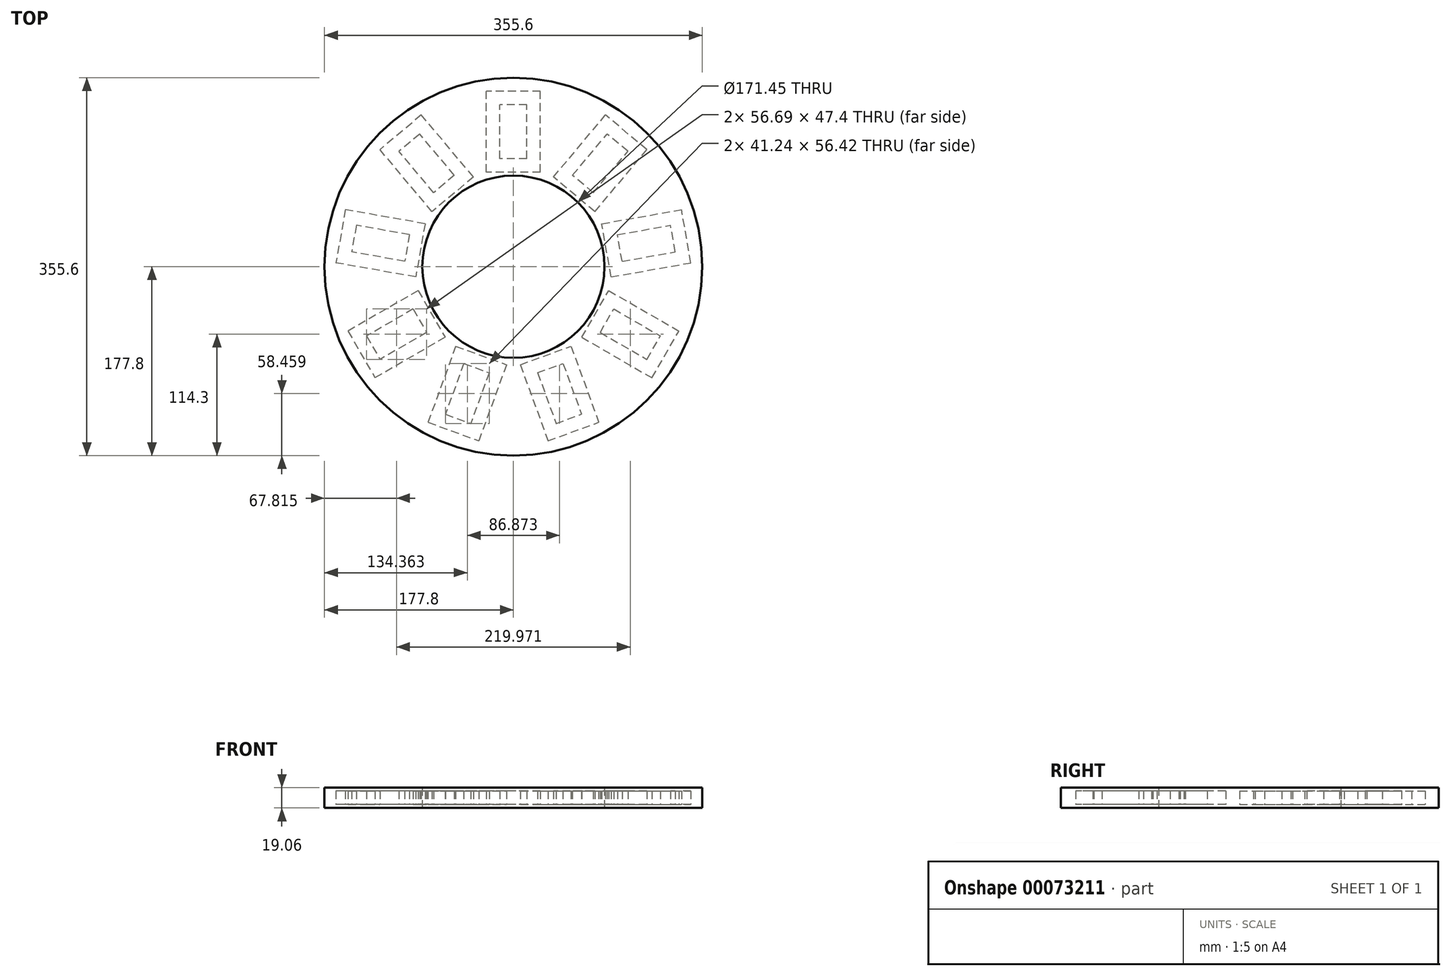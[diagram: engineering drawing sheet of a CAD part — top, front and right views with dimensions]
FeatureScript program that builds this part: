
annotation { "Feature Type Name" : "Feature", "Feature Type Description" : "" }
export const myFeature = defineFeature(function(context is Context, id is Id, definition is map)
    precondition{}
    {
        {
            var Q0;
            Q0=qCreatedBy(makeId("Top.planeOp"),FACE);
            var sketch = newSketch(context, id + "F0", { "sketchPlane" : qUnion([Q0])});
            skCircle(sketch, "E0", {"center": v(0, 0) * mm, "radius": 85.73 * mm, "construction": true});
            skCircle(sketch, "E1", {"center": v(0, 0) * mm, "radius": 177.8 * mm, "construction": true});
            skCircle(sketch, "E2", {"center": v(0, 0) * mm, "radius": 101.6 * mm, "construction": true});
            skCircle(sketch, "E3", {"center": v(0, 0) * mm, "radius": 152.4 * mm, "construction": true});
            skLineSegment(sketch, "E4.rect.bottom", {"start": v(12.7, 101.6) * mm, "end": v(-12.7, 101.6) * mm});
            skLineSegment(sketch, "E4.rect.top", {"start": v(12.7, 152.4) * mm, "end": v(-12.7, 152.4) * mm});
            skLineSegment(sketch, "E4.rect.left", {"start": v(12.7, 101.6) * mm, "end": v(12.7, 152.4) * mm});
            skLineSegment(sketch, "E4.rect.right", {"start": v(-12.7, 101.6) * mm, "end": v(-12.7, 152.4) * mm});
            skPoint(sketch, "E4.rect.middle", {"position": v(0, 127) * mm});
            skLineSegment(sketch, "E5.rect.bottom", {"start": v(25.4, 88.9) * mm, "end": v(-25.4, 88.9) * mm});
            skLineSegment(sketch, "E5.rect.top", {"start": v(25.4, 165.1) * mm, "end": v(-25.4, 165.1) * mm});
            skLineSegment(sketch, "E5.rect.left", {"start": v(25.4, 88.9) * mm, "end": v(25.4, 165.1) * mm});
            skLineSegment(sketch, "E5.rect.right", {"start": v(-25.4, 88.9) * mm, "end": v(-25.4, 165.1) * mm});
            skLineSegment(sketch, "E6.1.0", {"start": v(-37.69, 84.43) * mm, "end": v(-76.6, 51.77) * mm});
            skLineSegment(sketch, "E6.1.1", {"start": v(-86.67, 142.8) * mm, "end": v(-125.58, 110.15) * mm});
            skLineSegment(sketch, "E6.1.2", {"start": v(-37.69, 84.43) * mm, "end": v(-86.67, 142.8) * mm});
            skLineSegment(sketch, "E6.1.3", {"start": v(-76.6, 51.77) * mm, "end": v(-125.58, 110.15) * mm});
            skPoint(sketch, "E6.1.4", {"position": v(-81.63, 97.29) * mm});
            skPoint(sketch, "E6.1.5", {"position": v(-81.63, 97.29) * mm});
            skLineSegment(sketch, "E6.2.0", {"start": v(-83.14, 40.45) * mm, "end": v(-91.96, -9.58) * mm});
            skLineSegment(sketch, "E6.2.1", {"start": v(-158.18, 53.68) * mm, "end": v(-167, 3.66) * mm});
            skLineSegment(sketch, "E6.2.2", {"start": v(-83.14, 40.45) * mm, "end": v(-158.18, 53.68) * mm});
            skLineSegment(sketch, "E6.2.3", {"start": v(-91.96, -9.58) * mm, "end": v(-167, 3.66) * mm});
            skPoint(sketch, "E6.2.4", {"position": v(-125.07, 22.05) * mm});
            skPoint(sketch, "E6.2.5", {"position": v(-125.07, 22.05) * mm});
            skLineSegment(sketch, "E6.3.0", {"start": v(-89.69, -22.45) * mm, "end": v(-64.29, -66.45) * mm});
            skLineSegment(sketch, "E6.3.1", {"start": v(-155.68, -60.55) * mm, "end": v(-130.28, -104.55) * mm});
            skLineSegment(sketch, "E6.3.2", {"start": v(-89.69, -22.45) * mm, "end": v(-155.68, -60.55) * mm});
            skLineSegment(sketch, "E6.3.3", {"start": v(-64.29, -66.45) * mm, "end": v(-130.28, -104.55) * mm});
            skPoint(sketch, "E6.3.4", {"position": v(-109.99, -63.5) * mm});
            skPoint(sketch, "E6.3.5", {"position": v(-109.99, -63.5) * mm});
            skLineSegment(sketch, "E6.4.0", {"start": v(-54.27, -74.85) * mm, "end": v(-6.54, -92.23) * mm});
            skLineSegment(sketch, "E6.4.1", {"start": v(-80.34, -146.46) * mm, "end": v(-32.6, -163.83) * mm});
            skLineSegment(sketch, "E6.4.2", {"start": v(-54.27, -74.85) * mm, "end": v(-80.34, -146.46) * mm});
            skLineSegment(sketch, "E6.4.3", {"start": v(-6.54, -92.23) * mm, "end": v(-32.6, -163.83) * mm});
            skPoint(sketch, "E6.4.4", {"position": v(-43.44, -119.34) * mm});
            skPoint(sketch, "E6.4.5", {"position": v(-43.44, -119.34) * mm});
            skLineSegment(sketch, "E6.5.0", {"start": v(6.54, -92.23) * mm, "end": v(54.27, -74.85) * mm});
            skLineSegment(sketch, "E6.5.1", {"start": v(32.6, -163.83) * mm, "end": v(80.34, -146.46) * mm});
            skLineSegment(sketch, "E6.5.2", {"start": v(6.54, -92.23) * mm, "end": v(32.6, -163.83) * mm});
            skLineSegment(sketch, "E6.5.3", {"start": v(54.27, -74.85) * mm, "end": v(80.34, -146.46) * mm});
            skPoint(sketch, "E6.5.4", {"position": v(43.44, -119.34) * mm});
            skPoint(sketch, "E6.5.5", {"position": v(43.44, -119.34) * mm});
            skLineSegment(sketch, "E6.6.0", {"start": v(64.29, -66.45) * mm, "end": v(89.69, -22.45) * mm});
            skLineSegment(sketch, "E6.6.1", {"start": v(130.28, -104.55) * mm, "end": v(155.68, -60.55) * mm});
            skLineSegment(sketch, "E6.6.2", {"start": v(64.29, -66.45) * mm, "end": v(130.28, -104.55) * mm});
            skLineSegment(sketch, "E6.6.3", {"start": v(89.69, -22.45) * mm, "end": v(155.68, -60.55) * mm});
            skPoint(sketch, "E6.6.4", {"position": v(109.99, -63.5) * mm});
            skPoint(sketch, "E6.6.5", {"position": v(109.99, -63.5) * mm});
            skLineSegment(sketch, "E6.7.0", {"start": v(91.96, -9.58) * mm, "end": v(83.14, 40.45) * mm});
            skLineSegment(sketch, "E6.7.1", {"start": v(167, 3.66) * mm, "end": v(158.18, 53.68) * mm});
            skLineSegment(sketch, "E6.7.2", {"start": v(91.96, -9.58) * mm, "end": v(167, 3.66) * mm});
            skLineSegment(sketch, "E6.7.3", {"start": v(83.14, 40.45) * mm, "end": v(158.18, 53.68) * mm});
            skPoint(sketch, "E6.7.4", {"position": v(125.07, 22.05) * mm});
            skPoint(sketch, "E6.7.5", {"position": v(125.07, 22.05) * mm});
            skLineSegment(sketch, "E6.8.0", {"start": v(76.6, 51.77) * mm, "end": v(37.69, 84.43) * mm});
            skLineSegment(sketch, "E6.8.1", {"start": v(125.58, 110.15) * mm, "end": v(86.67, 142.8) * mm});
            skLineSegment(sketch, "E6.8.2", {"start": v(76.6, 51.77) * mm, "end": v(125.58, 110.15) * mm});
            skLineSegment(sketch, "E6.8.3", {"start": v(37.69, 84.43) * mm, "end": v(86.67, 142.8) * mm});
            skPoint(sketch, "E6.8.4", {"position": v(81.63, 97.29) * mm});
            skPoint(sketch, "E6.8.5", {"position": v(81.63, 97.29) * mm});
            skLineSegment(sketch, "E7.1.0", {"start": v(-88.23, 124.9) * mm, "end": v(-107.69, 108.58) * mm});
            skLineSegment(sketch, "E7.1.1", {"start": v(-75.04, 69.67) * mm, "end": v(-107.69, 108.58) * mm});
            skLineSegment(sketch, "E7.1.2", {"start": v(-55.58, 86) * mm, "end": v(-88.23, 124.9) * mm});
            skLineSegment(sketch, "E7.1.3", {"start": v(-55.58, 86) * mm, "end": v(-75.04, 69.67) * mm});
            skLineSegment(sketch, "E7.2.0", {"start": v(-147.88, 38.97) * mm, "end": v(-152.3, 13.96) * mm});
            skLineSegment(sketch, "E7.2.1", {"start": v(-102.26, 5.14) * mm, "end": v(-152.3, 13.96) * mm});
            skLineSegment(sketch, "E7.2.2", {"start": v(-97.85, 30.15) * mm, "end": v(-147.88, 38.97) * mm});
            skLineSegment(sketch, "E7.2.3", {"start": v(-97.85, 30.15) * mm, "end": v(-102.26, 5.14) * mm});
            skLineSegment(sketch, "E7.3.0", {"start": v(-138.33, -65.2) * mm, "end": v(-125.63, -87.2) * mm});
            skLineSegment(sketch, "E7.3.1", {"start": v(-81.64, -61.8) * mm, "end": v(-125.63, -87.2) * mm});
            skLineSegment(sketch, "E7.3.2", {"start": v(-94.34, -39.8) * mm, "end": v(-138.33, -65.2) * mm});
            skLineSegment(sketch, "E7.3.3", {"start": v(-94.34, -39.8) * mm, "end": v(-81.64, -61.8) * mm});
            skLineSegment(sketch, "E7.4.0", {"start": v(-64.06, -138.87) * mm, "end": v(-40.19, -147.55) * mm});
            skLineSegment(sketch, "E7.4.1", {"start": v(-22.82, -99.82) * mm, "end": v(-40.19, -147.55) * mm});
            skLineSegment(sketch, "E7.4.2", {"start": v(-46.68, -91.13) * mm, "end": v(-64.06, -138.87) * mm});
            skLineSegment(sketch, "E7.4.3", {"start": v(-46.68, -91.13) * mm, "end": v(-22.82, -99.82) * mm});
            skLineSegment(sketch, "E7.5.0", {"start": v(40.19, -147.55) * mm, "end": v(64.06, -138.87) * mm});
            skLineSegment(sketch, "E7.5.1", {"start": v(46.68, -91.13) * mm, "end": v(64.06, -138.87) * mm});
            skLineSegment(sketch, "E7.5.2", {"start": v(22.82, -99.82) * mm, "end": v(40.19, -147.55) * mm});
            skLineSegment(sketch, "E7.5.3", {"start": v(22.82, -99.82) * mm, "end": v(46.68, -91.13) * mm});
            skLineSegment(sketch, "E7.6.0", {"start": v(125.63, -87.2) * mm, "end": v(138.33, -65.2) * mm});
            skLineSegment(sketch, "E7.6.1", {"start": v(94.34, -39.8) * mm, "end": v(138.33, -65.2) * mm});
            skLineSegment(sketch, "E7.6.2", {"start": v(81.64, -61.8) * mm, "end": v(125.63, -87.2) * mm});
            skLineSegment(sketch, "E7.6.3", {"start": v(81.64, -61.8) * mm, "end": v(94.34, -39.8) * mm});
            skLineSegment(sketch, "E7.7.0", {"start": v(152.3, 13.96) * mm, "end": v(147.88, 38.97) * mm});
            skLineSegment(sketch, "E7.7.1", {"start": v(97.85, 30.15) * mm, "end": v(147.88, 38.97) * mm});
            skLineSegment(sketch, "E7.7.2", {"start": v(102.26, 5.14) * mm, "end": v(152.3, 13.96) * mm});
            skLineSegment(sketch, "E7.7.3", {"start": v(102.26, 5.14) * mm, "end": v(97.85, 30.15) * mm});
            skLineSegment(sketch, "E7.8.0", {"start": v(107.69, 108.58) * mm, "end": v(88.23, 124.9) * mm});
            skLineSegment(sketch, "E7.8.1", {"start": v(55.58, 86) * mm, "end": v(88.23, 124.9) * mm});
            skLineSegment(sketch, "E7.8.2", {"start": v(75.04, 69.67) * mm, "end": v(107.69, 108.58) * mm});
            skLineSegment(sketch, "E7.8.3", {"start": v(75.04, 69.67) * mm, "end": v(55.58, 86) * mm});
            skSolve(sketch);
        }
        {
            var Q0;
            Q0=makeQuery(id+"F0.imprint","IMPRINT",FACE,{"disambiguationData":[TD([[makeQuery(id+"F0.imprint","IMPRINT",EDGE,{"derivedFrom":sQuery(id+"F0.wireOp",EDGE,"E6.1.0")}),-1.0]])]});
            var Q1;
            Q1=makeQuery(id+"F0.imprint","IMPRINT",FACE,{"disambiguationData":[TD([[makeQuery(id+"F0.imprint","IMPRINT",EDGE,{"derivedFrom":sQuery(id+"F0.wireOp",EDGE,"E4.rect.bottom")}),1.0]])]});
            var Q2;
            Q2=makeQuery(id+"F0.imprint","IMPRINT",FACE,{"disambiguationData":[TD([[makeQuery(id+"F0.imprint","IMPRINT",EDGE,{"derivedFrom":sQuery(id+"F0.wireOp",EDGE,"E6.9.0")}),-1.0]])]});
            var Q3;
            Q3=makeQuery(id+"F0.imprint","IMPRINT",FACE,{"disambiguationData":[TD([[makeQuery(id+"F0.imprint","IMPRINT",EDGE,{"derivedFrom":sQuery(id+"F0.wireOp",EDGE,"E6.2.0")}),-1.0]])]});
            var Q4;
            Q4=makeQuery(id+"F0.imprint","IMPRINT",FACE,{"disambiguationData":[TD([[makeQuery(id+"F0.imprint","IMPRINT",EDGE,{"derivedFrom":sQuery(id+"F0.wireOp",EDGE,"E6.8.0")}),-1.0]])]});
            var Q5;
            Q5=makeQuery(id+"F0.imprint","IMPRINT",FACE,{"disambiguationData":[TD([[makeQuery(id+"F0.imprint","IMPRINT",EDGE,{"derivedFrom":sQuery(id+"F0.wireOp",EDGE,"E6.7.0")}),-1.0]])]});
            var Q6;
            Q6=makeQuery(id+"F0.imprint","IMPRINT",FACE,{"disambiguationData":[TD([[makeQuery(id+"F0.imprint","IMPRINT",EDGE,{"derivedFrom":sQuery(id+"F0.wireOp",EDGE,"E6.6.0")}),-1.0]])]});
            var Q7;
            Q7=makeQuery(id+"F0.imprint","IMPRINT",FACE,{"disambiguationData":[TD([[makeQuery(id+"F0.imprint","IMPRINT",EDGE,{"derivedFrom":sQuery(id+"F0.wireOp",EDGE,"E6.5.0")}),-1.0]])]});
            var Q8;
            Q8=makeQuery(id+"F0.imprint","IMPRINT",FACE,{"disambiguationData":[TD([[makeQuery(id+"F0.imprint","IMPRINT",EDGE,{"derivedFrom":sQuery(id+"F0.wireOp",EDGE,"E6.4.0")}),-1.0]])]});
            var Q9;
            Q9=makeQuery(id+"F0.imprint","IMPRINT",FACE,{"disambiguationData":[TD([[makeQuery(id+"F0.imprint","IMPRINT",EDGE,{"derivedFrom":sQuery(id+"F0.wireOp",EDGE,"E6.3.0")}),-1.0]])]});
            extrude(context, id + "F1", {"entities" : qUnion([Q0, Q1, Q2, Q3, Q4, Q5, Q6, Q7, Q8, Q9]), "depth" : 12.7 * mm});
        }
        {
            var Q0;
            Q0=qCreatedBy(makeId("Top.planeOp"),FACE);
            var sketch = newSketch(context, id + "F2", { "sketchPlane" : qUnion([Q0])});
            skCircle(sketch, "E8", {"center": v(0, 0) * mm, "radius": 177.8 * mm});
            skCircle(sketch, "E9", {"center": v(0, 0) * mm, "radius": 85.73 * mm});
            skSolve(sketch);
        }
        {
            var Q0;
            Q0=makeQuery(id+"F2.imprint","IMPRINT",FACE,{"disambiguationData":[TD([[makeQuery(id+"F2.imprint","IMPRINT",EDGE,{"derivedFrom":sQuery(id+"F2.wireOp",EDGE,"E8")}),1.0]])]});
            extrude(context, id + "F3", {"entities" : qUnion([Q0]), "depth" : 15.88 * mm, "hasSecondDirection" : true, "secondDirectionOppositeDirection" : true, "secondDirectionDepth" : 3.17 * mm});
        }
    });
